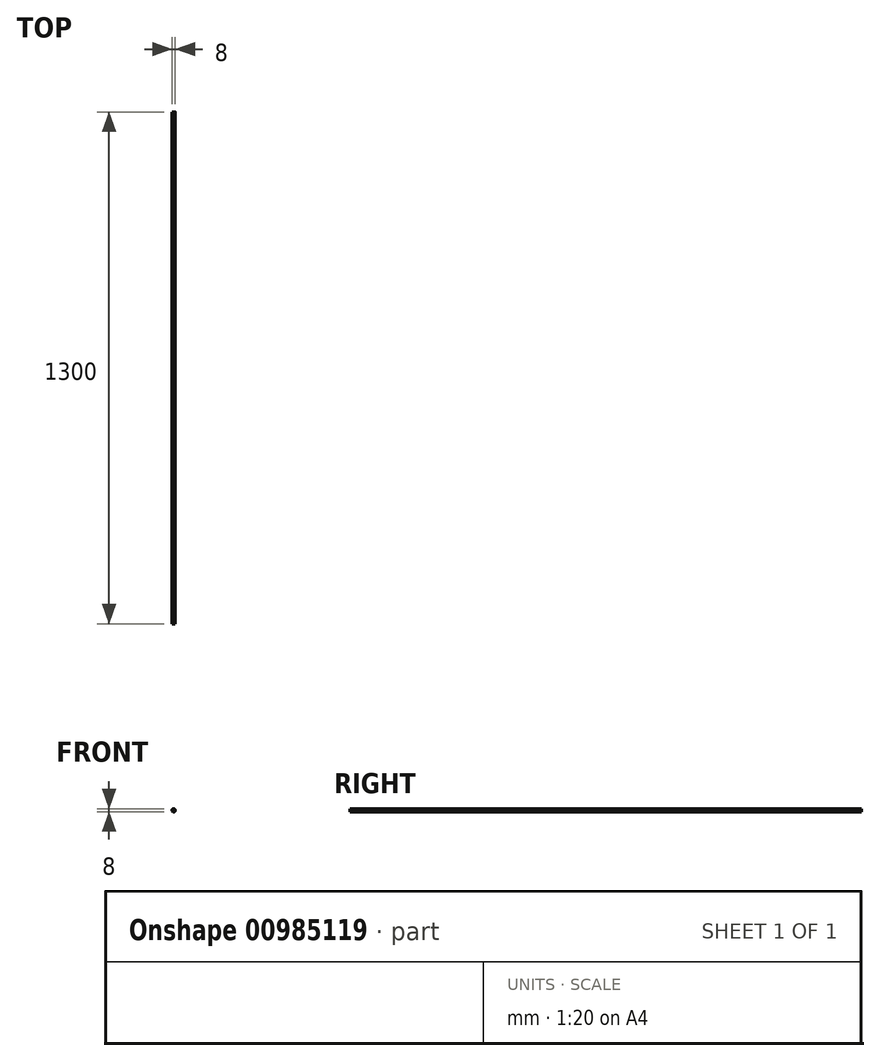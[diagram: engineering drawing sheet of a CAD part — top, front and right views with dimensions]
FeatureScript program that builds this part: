
annotation { "Feature Type Name" : "Feature", "Feature Type Description" : "" }
export const myFeature = defineFeature(function(context is Context, id is Id, definition is map)
    precondition{}
    {
        {
            var Q0;
            Q0=qCreatedBy(makeId("Front.planeOp"),FACE);
            var sketch = newSketch(context, id + "F0", { "sketchPlane" : qUnion([Q0])});
            skCircle(sketch, "E0", {"center": v(-34.88, 16.02) * mm, "radius": 4 * mm});
            skSolve(sketch);
        }
        {
            var Q0;
            Q0 = qSketchRegion(id + "F0", true);
            extrude(context, id + "F1", {"entities" : qUnion([Q0]), "depth" : 1300 * mm, "offsetDistance" : 25 * mm});
        }
    });
